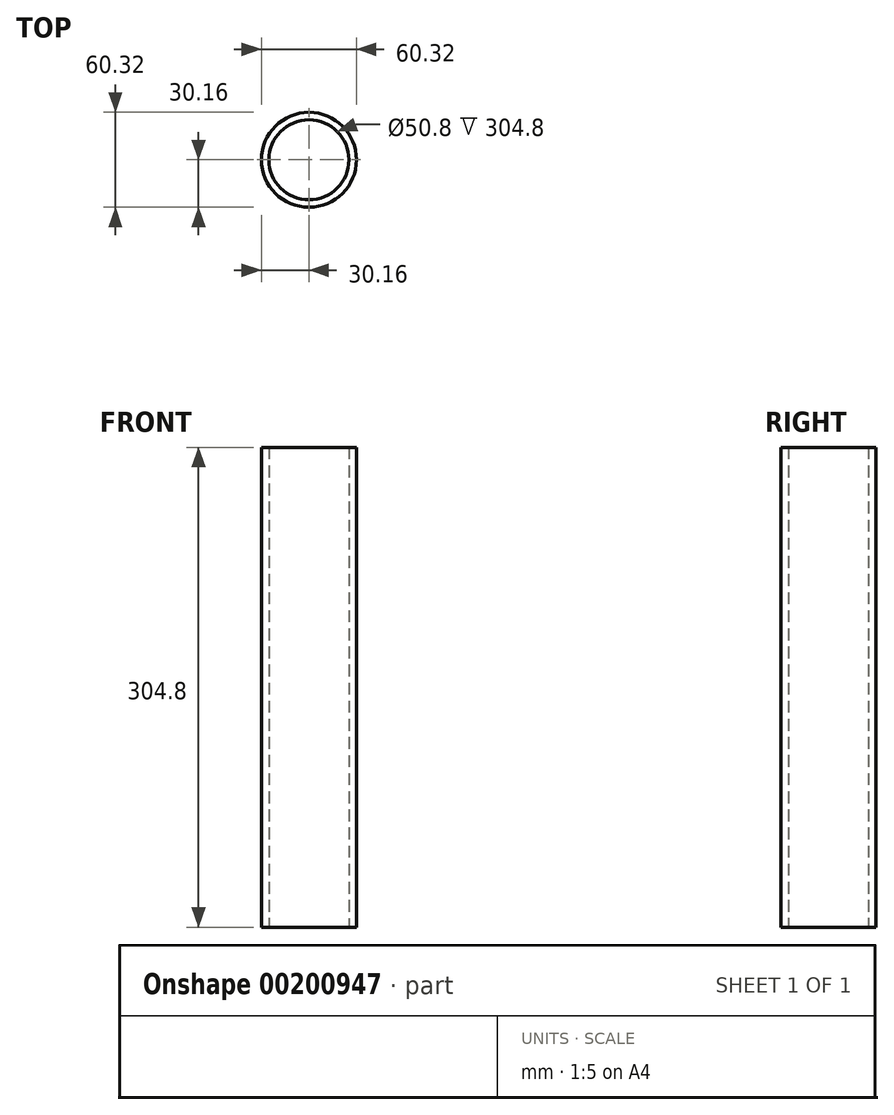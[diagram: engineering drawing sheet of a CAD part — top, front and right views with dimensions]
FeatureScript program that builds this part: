
annotation { "Feature Type Name" : "Feature", "Feature Type Description" : "" }
export const myFeature = defineFeature(function(context is Context, id is Id, definition is map)
    precondition{}
    {
        {
            var Q0;
            Q0=qCreatedBy(makeId("Top.planeOp"),FACE);
            var sketch = newSketch(context, id + "F0", { "sketchPlane" : qUnion([Q0])});
            skCircle(sketch, "E0", {"center": v(0, 0) * mm, "radius": 30.16 * mm});
            skCircle(sketch, "E1", {"center": v(0, 0) * mm, "radius": 25.4 * mm});
            skSolve(sketch);
        }
        {
            var Q0;
            Q0=makeQuery(id+"F0.imprint","IMPRINT",FACE,{"disambiguationData":[TD([[makeQuery(id+"F0.imprint","IMPRINT",EDGE,{"derivedFrom":sQuery(id+"F0.wireOp",EDGE,"E0")}),1.0]])]});
            extrude(context, id + "F1", {"entities" : qUnion([Q0]), "depth" : 304.8 * mm});
        }
    });
